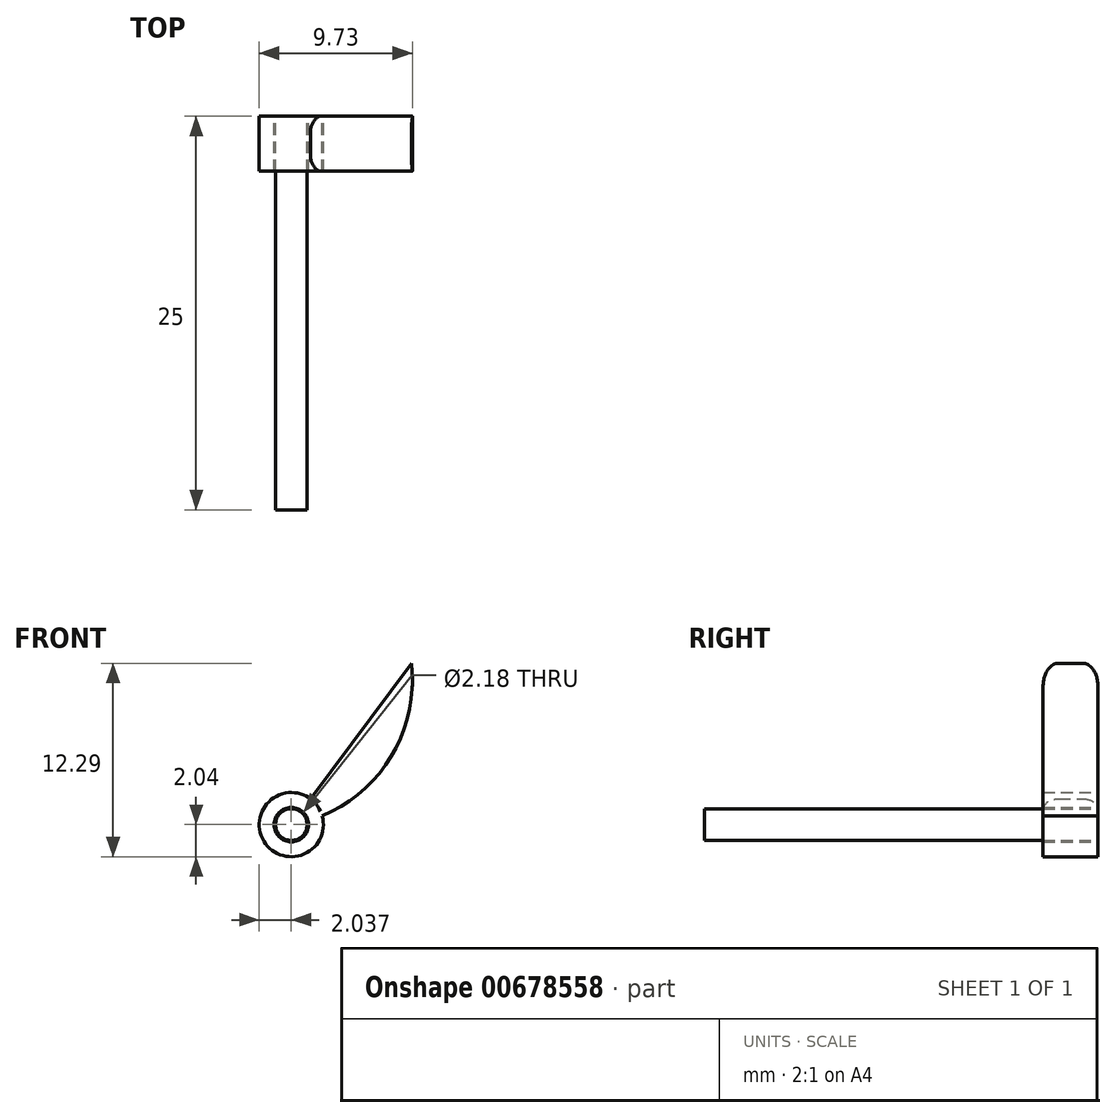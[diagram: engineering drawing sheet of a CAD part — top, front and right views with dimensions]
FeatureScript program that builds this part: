
annotation { "Feature Type Name" : "Feature", "Feature Type Description" : "" }
export const myFeature = defineFeature(function(context is Context, id is Id, definition is map)
    precondition{}
    {
        {
            var Q0;
            Q0=qCreatedBy(makeId("Front.planeOp"),FACE);
            var sketch = newSketch(context, id + "F0", { "sketchPlane" : qUnion([Q0])});
            skArc(sketch, "E0", {"start": v(2.09, 0) * mm, "mid": v(7.95, 3.6) * mm, "end": v(9.7, 10.25) * mm});
            skLineSegment(sketch, "E1", {"start": v(9.7, 10.25) * mm, "end": v(2.09, 0) * mm});
            skCircle(sketch, "E2", {"center": v(2.09, 0) * mm, "radius": 2.04 * mm});
            skSolve(sketch);
        }
        {
            var Q0;
            Q0 = qSketchRegion(id + "F0", true);
            extrude(context, id + "F1", {"entities" : qUnion([Q0]), "depth" : 3.5 * mm, "offsetDistance" : 25 * mm});
        }
        {
            var Q0;
            Q0=qCreatedBy(makeId("Front.planeOp"),FACE);
            var sketch = newSketch(context, id + "F2", { "sketchPlane" : qUnion([Q0])});
            skCircle(sketch, "E3", {"center": v(2.09, 0) * mm, "radius": 1.1 * mm});
            skSolve(sketch);
        }
        {
            var Q0;
            Q0 = qSketchRegion(id + "F2", true);
            extrude(context, id + "F3", {"entities" : qUnion([Q0]), "operationType" : NewBodyOperationType.REMOVE, "depth" : 59.1 * mm, "offsetDistance" : 25 * mm});
        }
        {
            var Q0;
            Q0=makeQuery(id+"F1.opExtrude","CAP_EDGE",EDGE,{"disambiguationData":[OSD([sQuery(id+"F0.wireOp",EDGE,"E1")])],"isStart":false});
            fillet(context, id + "F4", {"entities" : qUnion([Q0]), "radius" : 1 * mm, "tangentPropagation" : true, "allowEdgeOverflow" : false});
        }
        {
            var Q0;
            Q0=makeQuery(id+"F1.opExtrude","CAP_EDGE",EDGE,{"disambiguationData":[OSD([sQuery(id+"F0.wireOp",EDGE,"E1")])],"isStart":true});
            fillet(context, id + "F5", {"entities" : qUnion([Q0]), "radius" : 1 * mm, "tangentPropagation" : true, "allowEdgeOverflow" : false});
        }
        {
            var Q0;
            Q0=qCreatedBy(makeId("Front.planeOp"),FACE);
            var sketch = newSketch(context, id + "F6", { "sketchPlane" : qUnion([Q0])});
            skCircle(sketch, "E4", {"center": v(2.09, 0) * mm, "radius": 1 * mm});
            skSolve(sketch);
        }
        {
            var Q0;
            Q0 = qSketchRegion(id + "F6", true);
            extrude(context, id + "F7", {"entities" : qUnion([Q0]), "depth" : 25 * mm, "offsetDistance" : 25 * mm});
        }
    });
